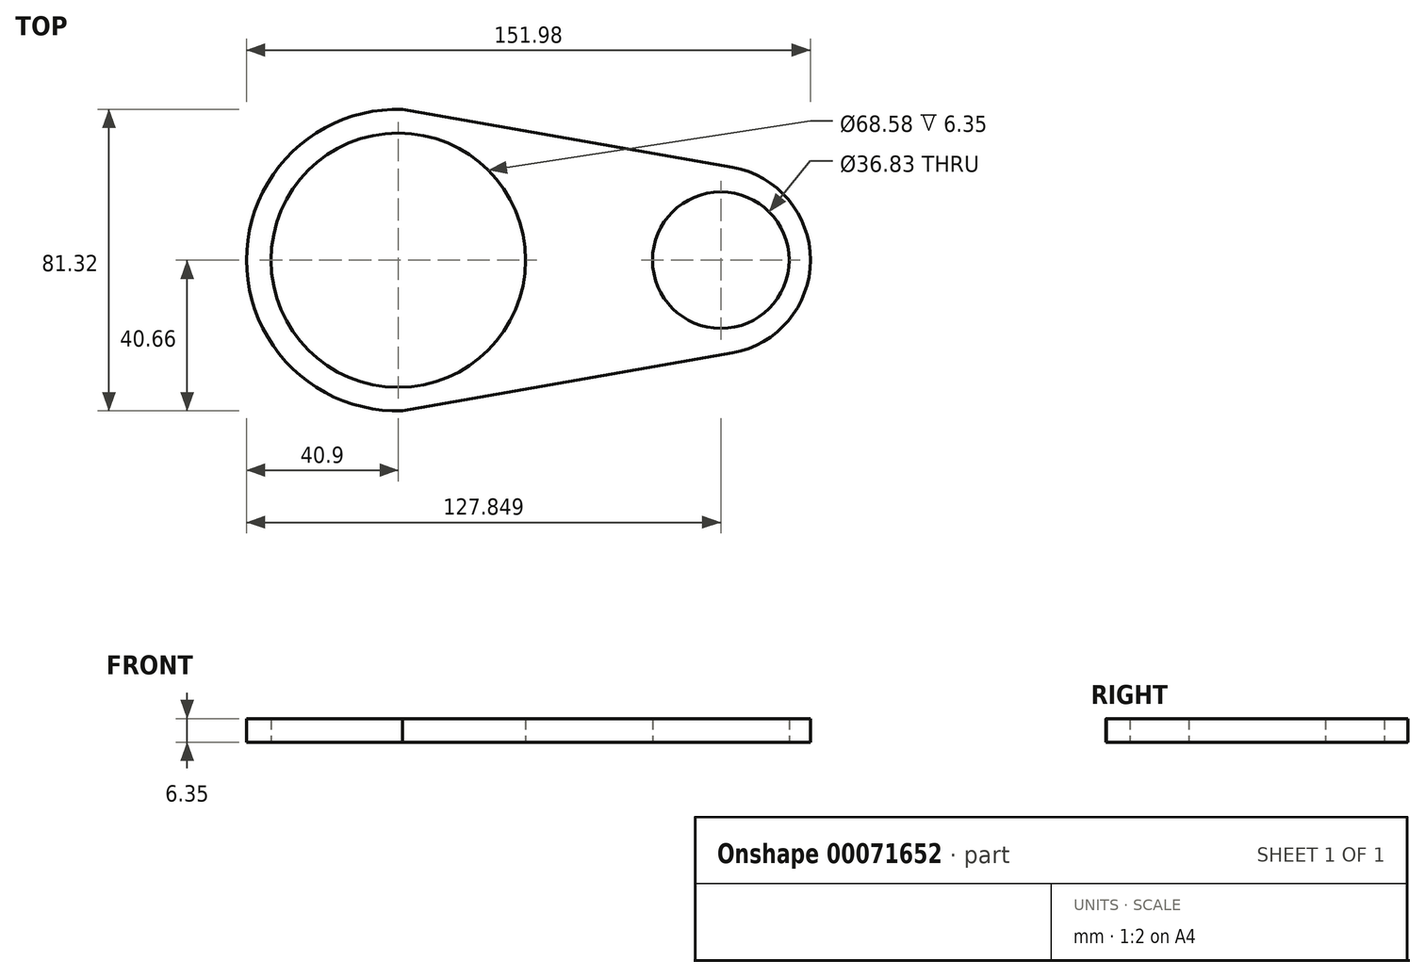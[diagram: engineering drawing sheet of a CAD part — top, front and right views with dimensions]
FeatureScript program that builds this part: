
annotation { "Feature Type Name" : "Feature", "Feature Type Description" : "" }
export const myFeature = defineFeature(function(context is Context, id is Id, definition is map)
    precondition{}
    {
        {
            var Q0;
            Q0=qCreatedBy(makeId("Top.planeOp"),FACE);
            var sketch = newSketch(context, id + "F0", { "sketchPlane" : qUnion([Q0])});
            skCircle(sketch, "E0", {"center": v(0, 0) * mm, "radius": 34.3 * mm});
            skCircle(sketch, "E1", {"center": v(86.95, 0) * mm, "radius": 18.41 * mm});
            skPoint(sketch, "E2", {"position": v(1.17, 40.64) * mm});
            skLineSegment(sketch, "E3", {"start": v(1.17, 40.64) * mm, "end": v(90.07, 25.02) * mm});
            skLineSegment(sketch, "E4", {"start": v(1.17, -40.64) * mm, "end": v(90.07, -25.02) * mm});
            skArc(sketch, "E5", {"start": v(90.07, -25.02) * mm, "mid": v(111.08, 0) * mm, "end": v(90.07, 25.02) * mm});
            skPoint(sketch, "E6.endSnap0", {"position": v(111.08, 0) * mm});
            skArc(sketch, "E7", {"start": v(1.17, 40.64) * mm, "mid": v(-40.9, 0) * mm, "end": v(1.17, -40.64) * mm});
            skLineSegment(sketch, "E8", {"start": v(0, 0) * mm, "end": v(86.95, 0) * mm});
            skLineSegment(sketch, "E9", {"start": v(-40.9, 0) * mm, "end": v(111.08, 0) * mm});
            skSolve(sketch);
        }
        {
            var Q0;
            Q0 = qSketchRegion(id + "F0", true);
            extrude(context, id + "F1", {"entities" : qUnion([Q0]), "depth" : 6.35 * mm});
        }
    });
